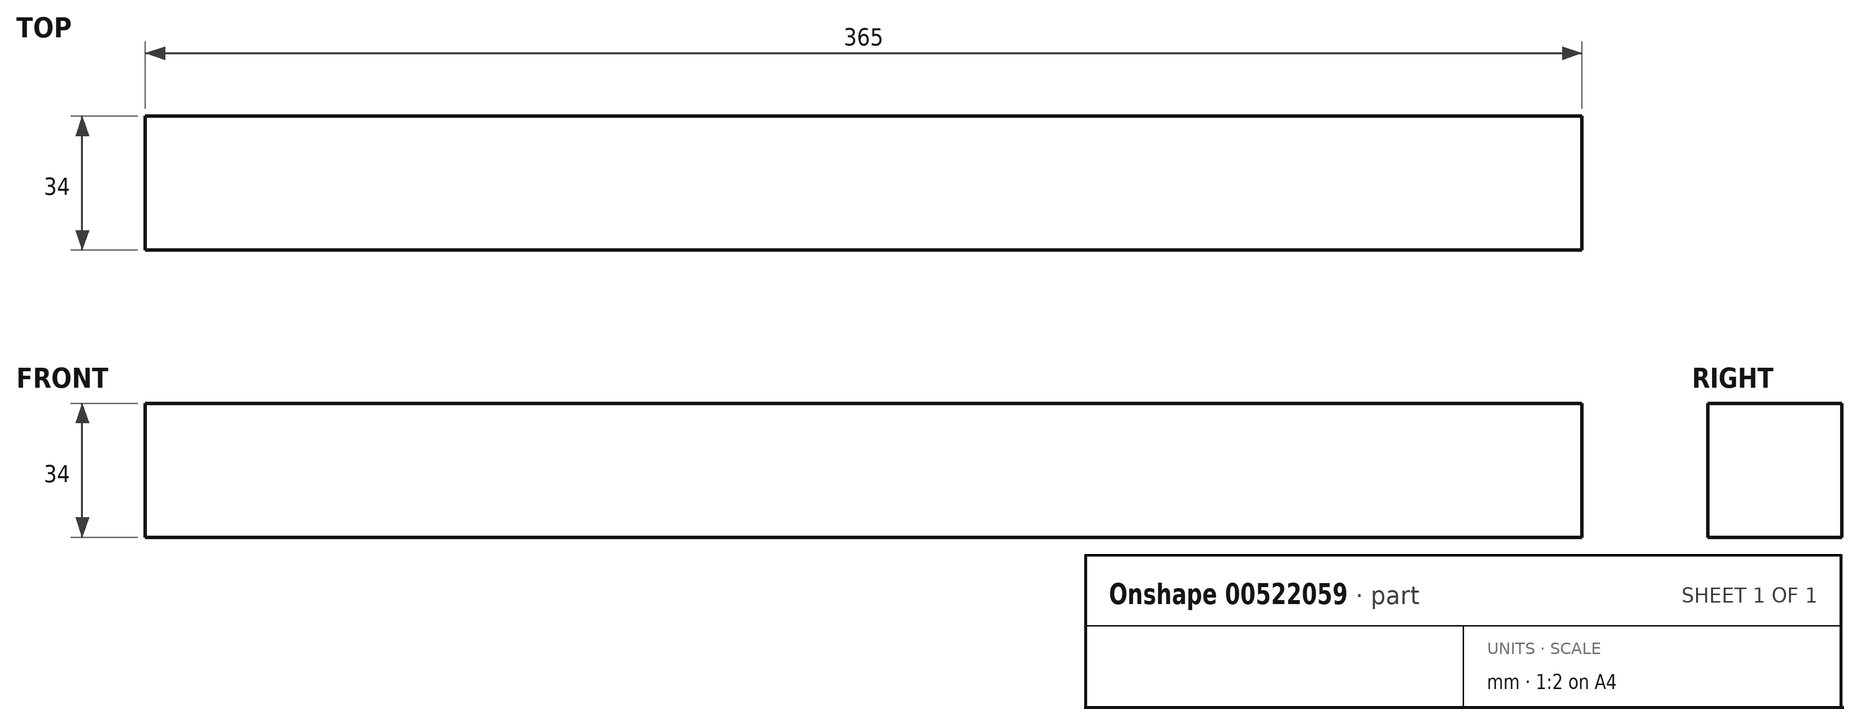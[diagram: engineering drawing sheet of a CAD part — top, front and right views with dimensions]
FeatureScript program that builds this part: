
annotation { "Feature Type Name" : "Feature", "Feature Type Description" : "" }
export const myFeature = defineFeature(function(context is Context, id is Id, definition is map)
    precondition{}
    {
        {
            var Q0;
            Q0=qCreatedBy(makeId("Right.planeOp"),FACE);
            var sketch = newSketch(context, id + "F0", { "sketchPlane" : qUnion([Q0])});
            skLineSegment(sketch, "E0.bottom", {"start": v(0, 0) * mm, "end": v(-34, 0) * mm});
            skLineSegment(sketch, "E0.top", {"start": v(0, 34) * mm, "end": v(-34, 34) * mm});
            skLineSegment(sketch, "E0.left", {"start": v(0, 0) * mm, "end": v(0, 34) * mm});
            skLineSegment(sketch, "E0.right", {"start": v(-34, 0) * mm, "end": v(-34, 34) * mm});
            skSolve(sketch);
        }
        {
            var Q0;
            Q0=makeQuery(id+"F0.imprint","IMPRINT",FACE,{"disambiguationData":[TD([[makeQuery(id+"F0.imprint","IMPRINT",EDGE,{"derivedFrom":sQuery(id+"F0.wireOp",EDGE,"E0.bottom")}),-1.0]])]});
            extrude(context, id + "F1", {"entities" : qUnion([Q0]), "oppositeDirection" : true, "depth" : 365 * mm, "offsetDistance" : 25 * mm});
        }
    });
